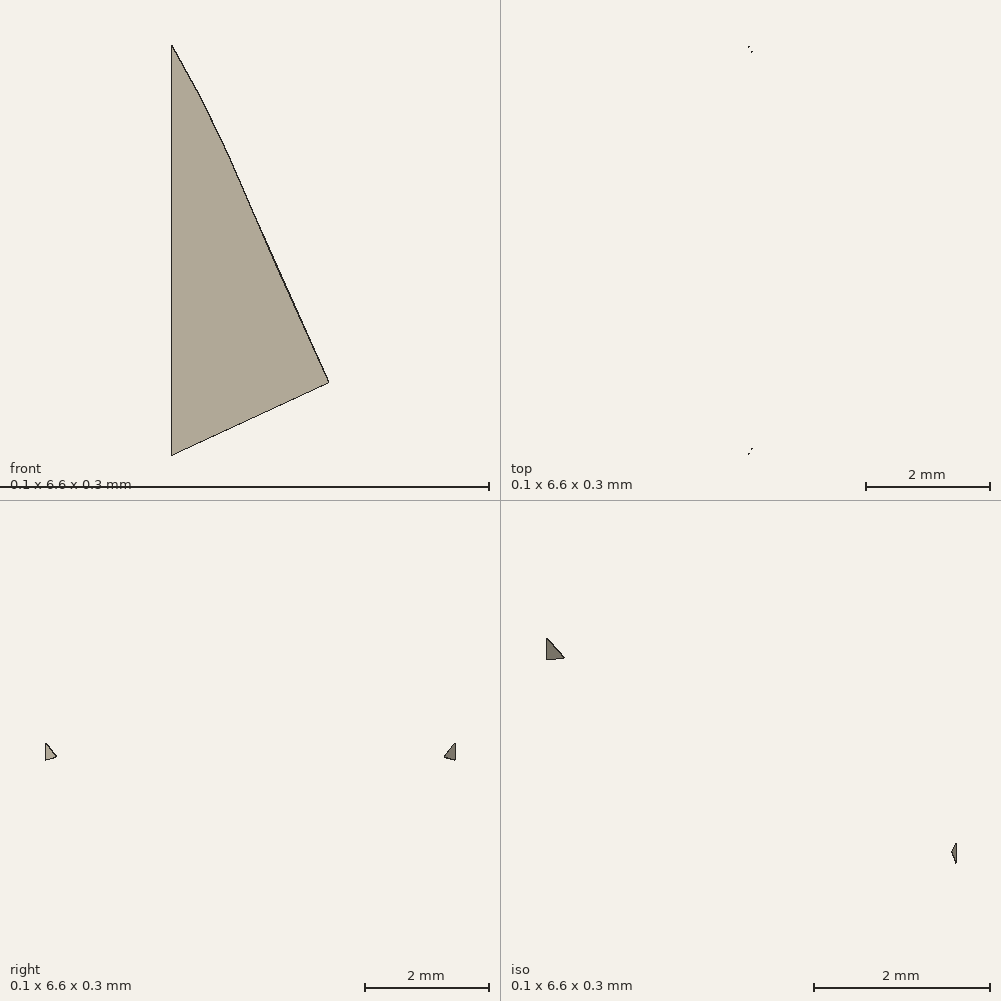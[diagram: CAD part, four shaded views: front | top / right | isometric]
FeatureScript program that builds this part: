
annotation { "Feature Type Name" : "Feature", "Feature Type Description" : "" }
export const myFeature = defineFeature(function(context is Context, id is Id, definition is map)
    precondition{}
    {
        {
            var Q0;
            Q0=qCreatedBy(makeId("Top.planeOp"),FACE);
            var sketch = newSketch(context, id + "F0", { "sketchPlane" : qUnion([Q0])});
            skLineSegment(sketch, "E0.bottom", {"start": v(103.53, -25.15) * mm, "end": v(-103.53, -25.15) * mm});
            skLineSegment(sketch, "E0.top", {"start": v(103.53, 25.15) * mm, "end": v(-103.53, 25.15) * mm});
            skLineSegment(sketch, "E0.left", {"start": v(103.53, -25.15) * mm, "end": v(103.53, 25.15) * mm});
            skLineSegment(sketch, "E0.right", {"start": v(-103.53, -25.15) * mm, "end": v(-103.53, 25.15) * mm});
            skPoint(sketch, "E0.middle", {"position": v(0, 0) * mm});
            skSolve(sketch);
        }
        {
            var Q0;
            Q0=makeQuery(id+"F0.imprint","IMPRINT",FACE,{"disambiguationData":[TD([[makeQuery(id+"F0.imprint","IMPRINT",EDGE,{"derivedFrom":sQuery(id+"F0.wireOp",EDGE,"E0.bottom")}),-1.0]])]});
            extrude(context, id + "F1", {"entities" : qUnion([Q0]), "endBound" : BoundingType.SYMMETRIC, "depth" : 50.8 * mm});
        }
        {
            var Q0;
            Q0=makeQuery(id+"F1.opExtrude","CAP_FACE",FACE,{"disambiguationData":[OSD([sQuery(id+"F0.wireOp",EDGE,"E0.bottom"),sQuery(id+"F0.wireOp",EDGE,"E0.top"),sQuery(id+"F0.wireOp",EDGE,"E0.left"),sQuery(id+"F0.wireOp",EDGE,"E0.right")])],"isStart":false});
            var sketch = newSketch(context, id + "F2", { "sketchPlane" : qUnion([Q0])});
            skFitSpline(sketch, "E1", {"points": [v(96.83, 0) * mm, v(92.01, 7.72) * mm, v(88.87, 8.55) * mm, v(-28.8, 2.06) * mm, v(-30.68, 3.11) * mm, v(-33, 9.31) * mm, v(-36.53, 11.43) * mm, v(-75.7, 9.81) * mm, v(-44.5, 7.5) * mm, v(-75.06, 3.11) * mm], "startDerivative": vector(-75.1, 124.39) * mm, "endDerivative": vector(-371.64, -30.61) * mm});
            skFitSpline(sketch, "E2", {"points": [v(-75.06, 3.11) * mm, v(-75.06, 2.58) * mm, v(-43.3, 0.62) * mm, v(-43.17, 0) * mm], "startDerivative": vector(-4.06, -5.49) * mm, "endDerivative": vector(3.76, 0) * mm});
            skFitSpline(sketch, "E3.MirrorCS", {"points": [v(96.83, 0) * mm, v(92.01, -7.72) * mm, v(88.87, -8.55) * mm, v(-28.8, -2.06) * mm, v(-30.68, -3.11) * mm, v(-33, -9.31) * mm, v(-36.53, -11.43) * mm, v(-75.7, -9.81) * mm, v(-44.5, -7.5) * mm, v(-75.06, -3.11) * mm], "startDerivative": vector(-75.1, -124.39) * mm, "endDerivative": vector(-371.64, 30.61) * mm});
            skFitSpline(sketch, "E4.MirrorCS", {"points": [v(-75.06, -3.11) * mm, v(-75.06, -2.58) * mm, v(-43.3, -0.62) * mm, v(-43.17, 0) * mm], "startDerivative": vector(-4.06, 5.49) * mm, "endDerivative": vector(3.76, 0) * mm});
            skArc(sketch, "E5.filletArc", {"start": v(94.82, -3.3) * mm, "mid": v(95.75, 0) * mm, "end": v(94.82, 3.3) * mm});
            skSolve(sketch);
        }
        {
            var Q0;
            Q0=makeQuery(id+"F2.imprint","IMPRINT",FACE,{"disambiguationData":[TD([[makeQuery(id+"F2.imprint","IMPRINT",EDGE,{"derivedFrom":sQuery(id+"F2.wireOp",EDGE,"E1")}),1.0]])]});
            extrude(context, id + "F3", {"entities" : qUnion([Q0]), "operationType" : NewBodyOperationType.INTERSECT, "endBound" : BoundingType.SYMMETRIC, "depth" : 50.8 * mm});
        }
        {
            var Q0;
            Q0=qCreatedBy(makeId("Top.planeOp"),FACE);
            cPlane(context, id + "F4", {"entities" : qUnion([Q0]), "cplaneType" : CPlaneType.OFFSET, "offset" : 12.7 * mm, "width" : 152.4 * mm, "height" : 152.4 * mm});
        }
        {
            var Q0;
            Q0=qCreatedBy(makeId("Front.planeOp"),FACE);
            var sketch = newSketch(context, id + "F5", { "sketchPlane" : qUnion([Q0])});
            skFitSpline(sketch, "E6", {"points": [v(-74.66, 14.17) * mm, v(-50.4, 11.79) * mm, v(-29.12, 13.57) * mm, v(13.44, 11.98) * mm, v(73.9, 13.38) * mm, v(93.38, 15.17) * mm, v(93.78, 14.77) * mm], "startDerivative": vector(147.7, -22.15) * mm, "endDerivative": vector(8.12, -17.56) * mm});
            skFitSpline(sketch, "E7.0", {"points": [v(-74.47, 15.43) * mm, v(-72.93, 15.2) * mm, v(-69.86, 14.74) * mm, v(-65.3, 14.1) * mm, v(-60.8, 13.56) * mm, v(-56.43, 13.18) * mm, v(-52.9, 13.04) * mm, v(-50.17, 13.05) * mm, v(-47.5, 13.15) * mm, v(-44.2, 13.41) * mm, v(-40.22, 13.86) * mm, v(-36.1, 14.33) * mm, v(-32.45, 14.66) * mm, v(-29.35, 14.85) * mm, v(-26.13, 14.95) * mm, v(-21.88, 14.95) * mm, v(-16.44, 14.8) * mm, v(-10.67, 14.52) * mm, v(-4.6, 14.17) * mm, v(1.79, 13.8) * mm, v(8.44, 13.45) * mm, v(15.36, 13.17) * mm, v(22.51, 12.98) * mm, v(32.25, 12.86) * mm, v(42.11, 12.94) * mm, v(51.77, 13.22) * mm, v(58.82, 13.53) * mm, v(65.6, 13.94) * mm, v(70.95, 14.36) * mm, v(75, 14.76) * mm, v(77.93, 15.08) * mm, v(80.7, 15.4) * mm, v(83.28, 15.7) * mm, v(85.64, 16) * mm, v(87.77, 16.24) * mm, v(89.32, 16.4) * mm, v(90.4, 16.49) * mm, v(91.16, 16.54) * mm, v(91.83, 16.57) * mm, v(92.43, 16.57) * mm, v(92.87, 16.55) * mm, v(93.21, 16.5) * mm, v(93.46, 16.46) * mm, v(93.71, 16.4) * mm, v(93.99, 16.3) * mm, v(94.25, 16.15) * mm, v(94.49, 15.96) * mm, v(94.68, 15.75) * mm, v(94.85, 15.48) * mm, v(94.91, 15.35) * mm, v(94.93, 15.3) * mm]});
            skFitSpline(sketch, "E8", {"points": [v(93.78, 14.77) * mm, v(94.93, 15.3) * mm], "startDerivative": vector(1.15, 0.53) * mm, "endDerivative": vector(1.15, 0.53) * mm});
            skFitSpline(sketch, "E9", {"points": [v(-74.66, 14.17) * mm, v(-75.12, 14.77) * mm, v(-74.47, 15.43) * mm], "startDerivative": vector(-1.51, 1.26) * mm, "endDerivative": vector(1.83, 1.25) * mm});
            skSolve(sketch);
        }
        {
            var Q0;
            Q0 = qSketchRegion(id + "F5", true);
            extrude(context, id + "F6", {"entities" : qUnion([Q0]), "operationType" : NewBodyOperationType.INTERSECT, "endBound" : BoundingType.SYMMETRIC, "depth" : 25.4 * mm});
        }
    });
